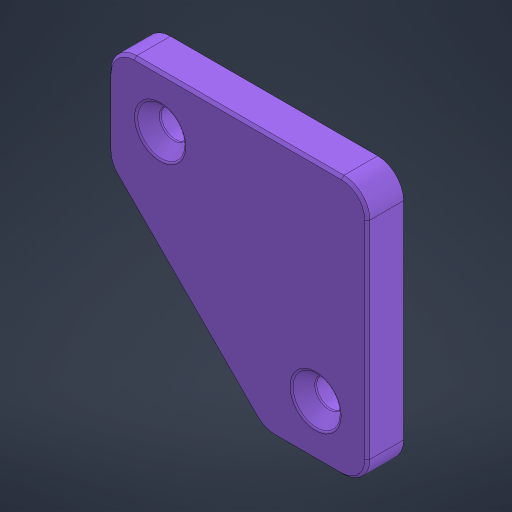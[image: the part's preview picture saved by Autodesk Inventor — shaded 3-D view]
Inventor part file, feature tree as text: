
AUTODESK INVENTOR PART (.ipt)
format: ipt  version: 2024 (Build 280153000, 153)  size: 293,888 bytes
history: native  units: mm
features: other x6, extrude x5, sketch x5, chamfer x4, fillet x4
ambient origin geometry x8: Origin, YZ Plane, XZ Plane, XY Plane, X Axis, Y Axis, Z Axis, Center Point
bodies: Body1 (feature_tree)
feature tree (24):
  other  "솔리드1"
  extrude  "돌출1"  Depth=50.0mm
  extrude  "돌출2"  Depth=50.0mm
  chamfer  "모따기2"  Distance=20.0mm
  fillet  "모깎기3"  Radius=20.0mm
  chamfer  "모따기3"  Distance=7.0mm
  fillet  "모깎기4"  Radius=10.0mm
  extrude  "돌출3"  Depth=10.0mm
  extrude  "돌출4"  Depth=10.0mm
  chamfer  "모따기4"  Distance=10.0mm
  fillet  "모깎기5"  Radius=5.4mm
  fillet  "모깎기6"  Radius=5.4mm
  chamfer  "모따기5"  Distance=10.0mm
  extrude  "돌출5"  Depth=2.0mm
  sketch  "스케치1"
  sketch  "스케치2"
  sketch  "스케치3"
  sketch  "스케치4"
  sketch  "스케치6"
  other  "Finish1"
  other  "Finish2"
  other  "Finish3"
  other  "Finish4"
  other  "Finish5"
